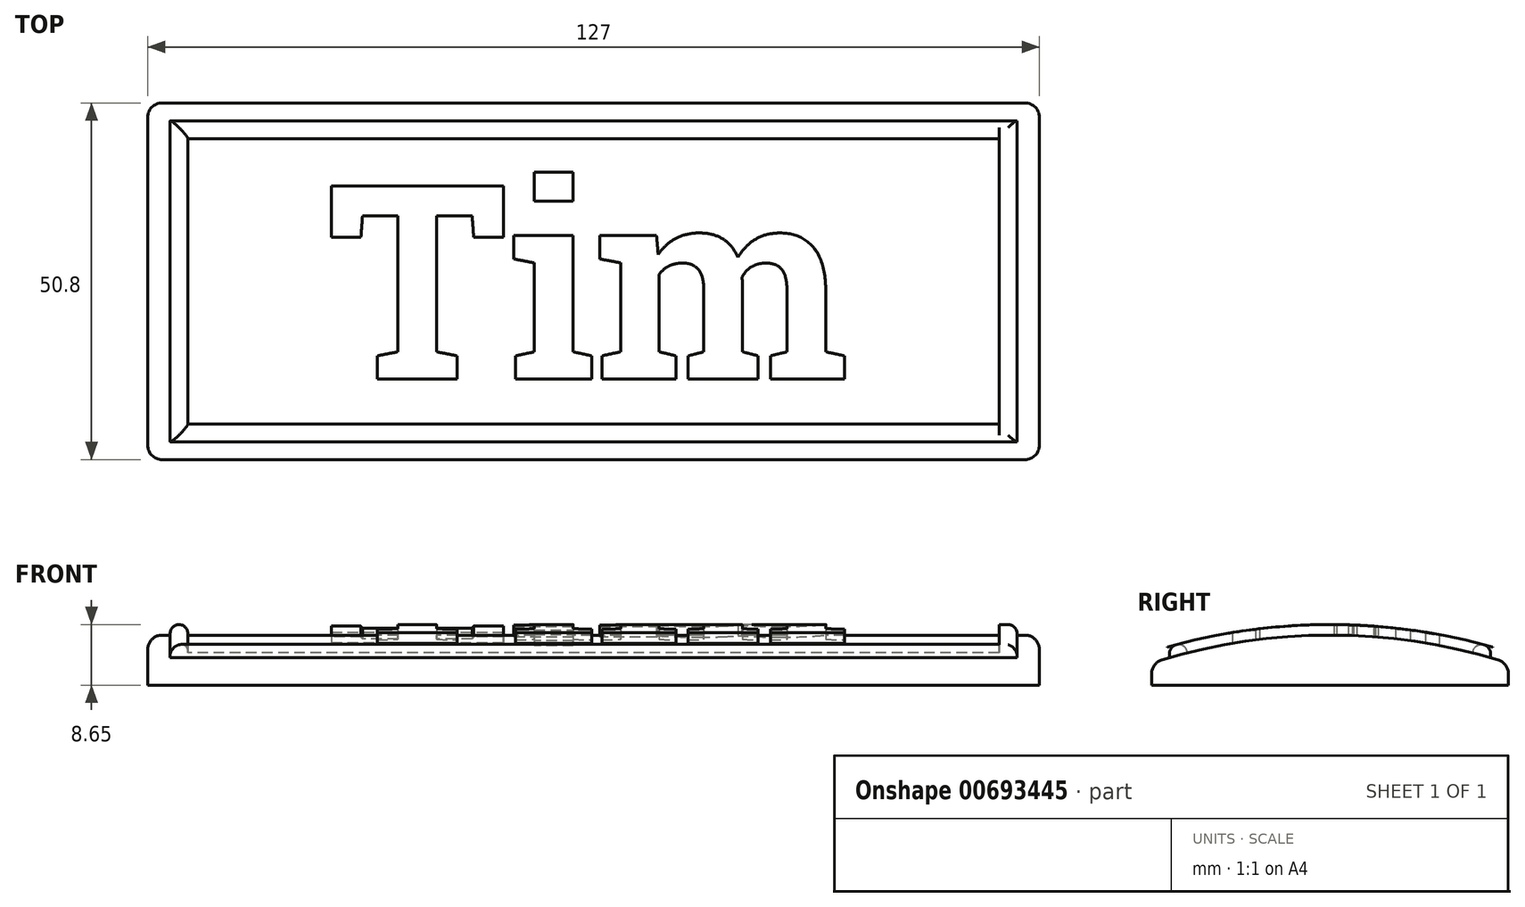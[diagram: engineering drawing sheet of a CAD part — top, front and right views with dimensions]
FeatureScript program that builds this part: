
annotation { "Feature Type Name" : "Feature", "Feature Type Description" : "" }
export const myFeature = defineFeature(function(context is Context, id is Id, definition is map)
    precondition{}
    {
        {
            var Q0;
            Q0=qCreatedBy(makeId("Right.planeOp"),FACE);
            var sketch = newSketch(context, id + "F0", { "sketchPlane" : qUnion([Q0])});
            skLineSegment(sketch, "E0", {"start": v(-46.49, 0) * mm, "end": v(44.71, 0) * mm, "construction": true});
            skLineSegment(sketch, "E1", {"start": v(0, 40.32) * mm, "end": v(0, -41.72) * mm, "construction": true});
            skPoint(sketch, "E2", {"position": v(0, -76.2) * mm});
            skLineSegment(sketch, "E3.top", {"start": v(-25.4, 0) * mm, "end": v(25.4, 0) * mm});
            skLineSegment(sketch, "E3.left", {"start": v(-25.4, 3.18) * mm, "end": v(-25.4, 0) * mm});
            skLineSegment(sketch, "E3.right", {"start": v(25.4, 3.18) * mm, "end": v(25.4, 0) * mm});
            skArc(sketch, "E4", {"start": v(25.4, 3.17) * mm, "mid": v(0, 7.14) * mm, "end": v(-25.4, 3.17) * mm});
            skSolve(sketch);
        }
        {
            var Q0;
            Q0 = qSketchRegion(id + "F0", true);
            extrude(context, id + "F1", {"entities" : qUnion([Q0]), "endBound" : BoundingType.SYMMETRIC, "depth" : 127 * mm, "offsetDistance" : 25.4 * mm});
        }
        {
            var Q0;
            Q0=qCreatedBy(makeId("Top.planeOp"),FACE);
            var sketch = newSketch(context, id + "F2", { "sketchPlane" : qUnion([Q0])});
            skText(sketch, "E5", { "text": "Tim", "fontName": "RobotoSlab-Bold.ttf"});
            const initialGuessF2  = {"E5": [-0.0381, -0.01392, 1, 0, 0.02784]};
            skSetInitialGuess(sketch, initialGuessF2);
            skSolve(sketch);
        }
        {
            var Q0;
            Q0 = qSketchRegion(id + "F2", true);
            extrude(context, id + "F3", {"entities" : qUnion([Q0]), "operationType" : NewBodyOperationType.ADD, "depth" : 25.4 * mm, "offsetDistance" : 25.4 * mm});
        }
        {
            var Q0;
            Q0=qCreatedBy(makeId("Top.planeOp"),FACE);
            var sketch = newSketch(context, id + "F4", { "sketchPlane" : qUnion([Q0])});
            skLineSegment(sketch, "E6.bottom", {"start": v(-60.33, 22.86) * mm, "end": v(60.33, 22.86) * mm});
            skLineSegment(sketch, "E6.top", {"start": v(-60.33, -22.86) * mm, "end": v(60.33, -22.86) * mm});
            skLineSegment(sketch, "E6.left", {"start": v(-60.33, 22.86) * mm, "end": v(-60.33, -22.86) * mm});
            skLineSegment(sketch, "E6.right", {"start": v(60.33, 22.86) * mm, "end": v(60.33, -22.86) * mm});
            skLineSegment(sketch, "E7.0", {"start": v(-57.79, 20.32) * mm, "end": v(-57.79, -20.32) * mm});
            skLineSegment(sketch, "E7.1", {"start": v(-57.79, 20.32) * mm, "end": v(57.79, 20.32) * mm});
            skLineSegment(sketch, "E7.2", {"start": v(57.79, 20.32) * mm, "end": v(57.79, -20.32) * mm});
            skLineSegment(sketch, "E7.3", {"start": v(-57.79, -20.32) * mm, "end": v(57.79, -20.32) * mm});
            skSolve(sketch);
        }
        {
            var Q0;
            Q0 = qSketchRegion(id + "F4", true);
            extrude(context, id + "F5", {"entities" : qUnion([Q0]), "operationType" : NewBodyOperationType.ADD, "depth" : 25.4 * mm, "offsetDistance" : 25.4 * mm});
        }
        {
            var Q0;
            Q0=qCreatedBy(makeId("Right.planeOp"),FACE);
            var sketch = newSketch(context, id + "F6", { "sketchPlane" : qUnion([Q0])});
            skLineSegment(sketch, "E8", {"start": v(-27.98, 0) * mm, "end": v(31.9, 0) * mm, "construction": true});
            skLineSegment(sketch, "E9", {"start": v(-27.98, 4.76) * mm, "end": v(40.05, 4.76) * mm, "construction": true});
            skPoint(sketch, "E10", {"position": v(-25.4, 4.76) * mm});
            skPoint(sketch, "E11", {"position": v(0, -76.2) * mm});
            skArc(sketch, "E12", {"start": v(46.3, -5.1) * mm, "mid": v(0.63, 8.65) * mm, "end": v(-45.24, -4.4) * mm});
            skLineSegment(sketch, "E13.bottom", {"start": v(-45.24, 65.78) * mm, "end": v(46.3, 65.78) * mm});
            skLineSegment(sketch, "E13.left", {"start": v(-45.24, 65.78) * mm, "end": v(-45.24, -4.4) * mm});
            skLineSegment(sketch, "E13.right", {"start": v(46.3, 65.78) * mm, "end": v(46.3, -5.1) * mm});
            skSolve(sketch);
        }
        {
            var Q0;
            Q0 = qSketchRegion(id + "F6", true);
            extrude(context, id + "F7", {"entities" : qUnion([Q0]), "operationType" : NewBodyOperationType.REMOVE, "endBound" : BoundingType.SYMMETRIC, "oppositeDirection" : true, "depth" : 152.4 * mm, "offsetDistance" : 25.4 * mm});
        }
        {
            var Q0;
            Q0=makeQuery(id+"F1.opExtrude","CAP_EDGE",EDGE,{"disambiguationData":[OSD([sQuery(id+"F0.wireOp",EDGE,"E4")])],"isStart":true});
            var Q1;
            Q1=makeQuery(id+"F1.opExtrude","SWEPT_EDGE",EDGE,{"disambiguationData":[OSD([sQuery(id+"F0.wireOp",EDGE,"E3.left"),sQuery(id+"F0.wireOp",EDGE,"E4")])]});
            var Q2;
            Q2=makeQuery(id+"F1.opExtrude","CAP_EDGE",EDGE,{"disambiguationData":[OSD([sQuery(id+"F0.wireOp",EDGE,"E4")])],"isStart":false});
            var Q3;
            Q3=makeQuery(id+"F1.opExtrude","SWEPT_EDGE",EDGE,{"disambiguationData":[OSD([sQuery(id+"F0.wireOp",EDGE,"E3.right"),sQuery(id+"F0.wireOp",EDGE,"E4")])]});
            var Q4;
            Q4=makeQuery(id+"F1.opExtrude","CAP_EDGE",EDGE,{"disambiguationData":[OSD([sQuery(id+"F0.wireOp",EDGE,"E3.left")])],"isStart":true});
            var Q5;
            Q5=makeQuery(id+"F1.opExtrude","CAP_EDGE",EDGE,{"disambiguationData":[OSD([sQuery(id+"F0.wireOp",EDGE,"E3.left")])],"isStart":false});
            var Q6;
            Q6=makeQuery(id+"F1.opExtrude","CAP_EDGE",EDGE,{"disambiguationData":[OSD([sQuery(id+"F0.wireOp",EDGE,"E3.right")])],"isStart":false});
            var Q7;
            Q7=makeQuery(id+"F1.opExtrude","CAP_EDGE",EDGE,{"disambiguationData":[OSD([sQuery(id+"F0.wireOp",EDGE,"E3.right")])],"isStart":true});
            fillet(context, id + "F8", {"entities" : qUnion([Q0, Q1, Q2, Q3, Q4, Q5, Q6, Q7]), "radius" : 2.03 * mm, "tangentPropagation" : true, "allowEdgeOverflow" : false});
        }
        {
            var Q0;
            Q0=makeQuery(id+"F7.boolean.opBoolean","INTERSECT",EDGE,{"derivedFrom":[makeQuery(id+"F5.opExtrude","SWEPT_FACE",FACE,{"disambiguationData":[OSD([sQuery(id+"F4.wireOp",EDGE,"E6.left")])]}),makeQuery(id+"F7.opExtrude","SWEPT_FACE",FACE,{"disambiguationData":[OSD([sQuery(id+"F6.wireOp",EDGE,"E12")])]})]});
            var Q1;
            Q1=makeQuery(id+"F7.boolean.opBoolean","INTERSECT",EDGE,{"derivedFrom":[makeQuery(id+"F5.opExtrude","SWEPT_FACE",FACE,{"disambiguationData":[OSD([sQuery(id+"F4.wireOp",EDGE,"E7.0")])]}),makeQuery(id+"F7.opExtrude","SWEPT_FACE",FACE,{"disambiguationData":[OSD([sQuery(id+"F6.wireOp",EDGE,"E12")])]})]});
            var Q2;
            Q2=makeQuery(id+"F7.boolean.opBoolean","INTERSECT",EDGE,{"derivedFrom":[makeQuery(id+"F5.opExtrude","SWEPT_FACE",FACE,{"disambiguationData":[OSD([sQuery(id+"F4.wireOp",EDGE,"E6.top")])]}),makeQuery(id+"F7.opExtrude","SWEPT_FACE",FACE,{"disambiguationData":[OSD([sQuery(id+"F6.wireOp",EDGE,"E12")])]})]});
            var Q3;
            Q3=makeQuery(id+"F7.boolean.opBoolean","INTERSECT",EDGE,{"derivedFrom":[makeQuery(id+"F5.opExtrude","SWEPT_FACE",FACE,{"disambiguationData":[OSD([sQuery(id+"F4.wireOp",EDGE,"E7.3")])]}),makeQuery(id+"F7.opExtrude","SWEPT_FACE",FACE,{"disambiguationData":[OSD([sQuery(id+"F6.wireOp",EDGE,"E12")])]})]});
            var Q4;
            Q4=makeQuery(id+"F7.boolean.opBoolean","INTERSECT",EDGE,{"derivedFrom":[makeQuery(id+"F5.opExtrude","SWEPT_FACE",FACE,{"disambiguationData":[OSD([sQuery(id+"F4.wireOp",EDGE,"E6.right")])]}),makeQuery(id+"F7.opExtrude","SWEPT_FACE",FACE,{"disambiguationData":[OSD([sQuery(id+"F6.wireOp",EDGE,"E12")])]})]});
            var Q5;
            Q5=makeQuery(id+"F7.boolean.opBoolean","INTERSECT",EDGE,{"derivedFrom":[makeQuery(id+"F5.opExtrude","SWEPT_FACE",FACE,{"disambiguationData":[OSD([sQuery(id+"F4.wireOp",EDGE,"E7.1")])]}),makeQuery(id+"F7.opExtrude","SWEPT_FACE",FACE,{"disambiguationData":[OSD([sQuery(id+"F6.wireOp",EDGE,"E12")])]})]});
            var Q6;
            Q6=makeQuery(id+"F7.boolean.opBoolean","INTERSECT",EDGE,{"derivedFrom":[makeQuery(id+"F5.opExtrude","SWEPT_FACE",FACE,{"disambiguationData":[OSD([sQuery(id+"F4.wireOp",EDGE,"E6.bottom")])]}),makeQuery(id+"F7.opExtrude","SWEPT_FACE",FACE,{"disambiguationData":[OSD([sQuery(id+"F6.wireOp",EDGE,"E12")])]})]});
            fillet(context, id + "F9", {"entities" : qUnion([Q0, Q1, Q2, Q3, Q4, Q5, Q6]), "radius" : 1.27 * mm, "tangentPropagation" : true, "allowEdgeOverflow" : false});
        }
    });
